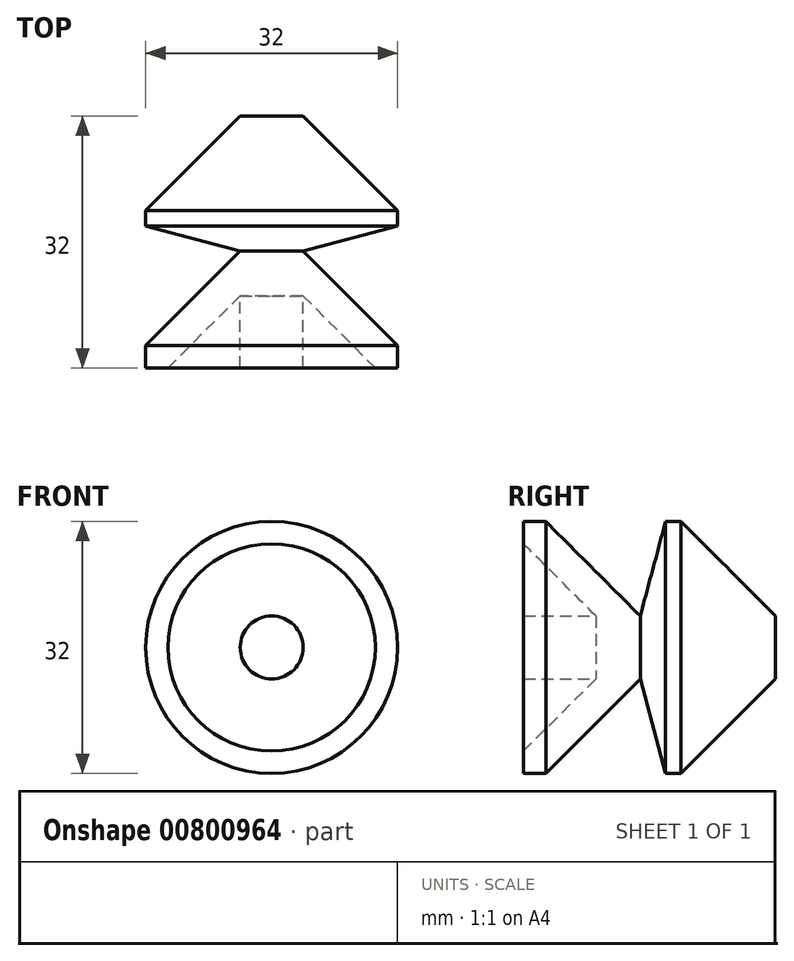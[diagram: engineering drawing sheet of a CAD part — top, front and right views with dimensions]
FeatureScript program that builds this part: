
annotation { "Feature Type Name" : "Feature", "Feature Type Description" : "" }
export const myFeature = defineFeature(function(context is Context, id is Id, definition is map)
    precondition{}
    {
        {
            var Q0;
            Q0=qCreatedBy(makeId("Top.planeOp"),FACE);
            var sketch = newSketch(context, id + "F0", { "sketchPlane" : qUnion([Q0])});
            skLineSegment(sketch, "E0", {"start": v(0, 0) * mm, "end": v(0, -32) * mm});
            skLineSegment(sketch, "E1", {"start": v(0, -32) * mm, "end": v(4, -32) * mm});
            skLineSegment(sketch, "E2", {"start": v(4, -32) * mm, "end": v(4, -22.83) * mm});
            skLineSegment(sketch, "E3", {"start": v(4, -22.83) * mm, "end": v(13.17, -32) * mm});
            skLineSegment(sketch, "E4", {"start": v(13.17, -32) * mm, "end": v(16, -32) * mm});
            skLineSegment(sketch, "E5", {"start": v(16, -32) * mm, "end": v(16, -29.17) * mm});
            skLineSegment(sketch, "E6", {"start": v(16, -29.17) * mm, "end": v(4, -17.17) * mm});
            skLineSegment(sketch, "E7", {"start": v(4, 0) * mm, "end": v(0, 0) * mm});
            skLineSegment(sketch, "E8", {"start": v(4, -5.66) * mm, "end": v(4, -13.03) * mm});
            skLineSegment(sketch, "E9", {"start": v(4, -13.03) * mm, "end": v(9.82, -11.47) * mm});
            skLineSegment(sketch, "E10", {"start": v(9.82, -11.47) * mm, "end": v(4, -5.66) * mm});
            skLineSegment(sketch, "E11", {"start": v(4, 0) * mm, "end": v(16, -12) * mm});
            skLineSegment(sketch, "E12", {"start": v(16, -12) * mm, "end": v(16, -13.96) * mm});
            skLineSegment(sketch, "E13", {"start": v(16, -13.96) * mm, "end": v(4, -17.17) * mm});
            skLineSegment(sketch, "E14", {"start": v(16, -29.17) * mm, "end": v(16, -13.96) * mm, "construction": true});
            skSolve(sketch);
        }
        {
            var Q0;
            Q0=makeQuery(id+"F0.imprint","IMPRINT",FACE,{"disambiguationData":[TD([[makeQuery(id+"F0.imprint","IMPRINT",EDGE,{"derivedFrom":sQuery(id+"F0.wireOp",EDGE,"E0")}),1.0]])]});
            var Q1;
            Q1=makeQuery(id+"F0.imprint","IMPRINT",FACE,{"disambiguationData":[TD([[makeQuery(id+"F0.imprint","IMPRINT",EDGE,{"derivedFrom":sQuery(id+"F0.wireOp",EDGE,"E8")}),1.0]])]});
            var Q2;
            Q2=sQuery(id+"F0.wireOp",EDGE,"E0");
            revolve(context, id + "F1", {"surfaceOperationType" : NewSurfaceOperationType.NEW, "entities" : qUnion([Q0, Q1]), "axis" : qUnion([Q2]), "revolveType" : RevolveType.FULL});
        }
    });
